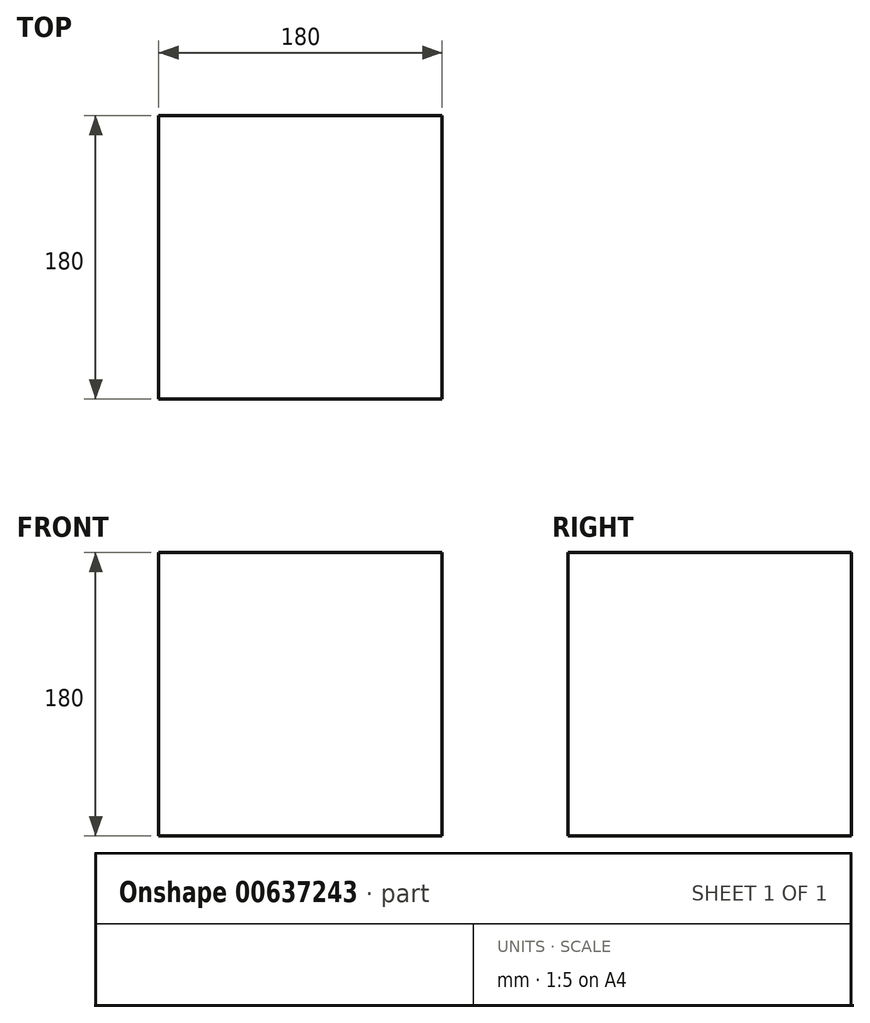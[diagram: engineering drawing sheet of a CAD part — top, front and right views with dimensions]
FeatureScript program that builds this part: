
annotation { "Feature Type Name" : "Feature", "Feature Type Description" : "" }
export const myFeature = defineFeature(function(context is Context, id is Id, definition is map)
    precondition{}
    {
        {
            var Q0;
            Q0=qCreatedBy(makeId("Top.planeOp"),FACE);
            var sketch = newSketch(context, id + "F0", { "sketchPlane" : qUnion([Q0])});
            skLineSegment(sketch, "E0.bottom", {"start": v(90, 90) * mm, "end": v(-90, 90) * mm});
            skLineSegment(sketch, "E0.top", {"start": v(90, -90) * mm, "end": v(-90, -90) * mm});
            skLineSegment(sketch, "E0.left", {"start": v(90, 90) * mm, "end": v(90, -90) * mm});
            skLineSegment(sketch, "E0.right", {"start": v(-90, 90) * mm, "end": v(-90, -90) * mm});
            skPoint(sketch, "E0.middle", {"position": v(0, 0) * mm});
            skSolve(sketch);
        }
        {
            var Q0;
            Q0=makeQuery(id+"F0.imprint","IMPRINT",FACE,{"disambiguationData":[TD([[makeQuery(id+"F0.imprint","IMPRINT",EDGE,{"derivedFrom":sQuery(id+"F0.wireOp",EDGE,"E0.bottom")}),1.0]])]});
            extrude(context, id + "F1", {"entities" : qUnion([Q0]), "depth" : 180 * mm, "offsetDistance" : 25 * mm});
        }
    });
